# Revit family: Sanitary_Toilet-Cisterns_Sanindusa_Urby-60-Cistern-With-Dual-Flush-Mechanism
name_source: partatom
category: Plumbing Fixtures
revit_build: Autodesk Revit 2018 (Build: 20170223_1515(x64)
units: mm (PartAtom-declared; Revit-internal decimal feet)

## family parameters
Always vertical = Yes
Cut with Voids When Loaded = No
Host = Wall
OmniClass Number = 23.45.00.00
OmniClass Title = Sanitary, Laundry, and Cleaning Equipment
Part Type = Normal
Room Calculation Point = No
Round Connector Dimension = Use Diameter
Shared = No

## types (1)
- SANINDUSA_Bottominletconnectioncisternwithdualflushmechanismforclosecoupledtoilet_140171004LM_379x155x432_Urb.y
    AssetType = Fixed
    CisternCapacity = 6 Lts
    CisternColor = white
    CisternHeight = LowLevel
    CisternMaterial = Vitreous China
    Color = white
    Constituents = Ceramic cistern with bottom inlet connection and dual flush mechanism included.
    Cost = 0 $
    Description = Bottom inlet connection cistern with dual flush mechanism for close coupled toilet
    Edition number = 1
    Element Type = CISTERN: A water storage unit attached to a sanitary terminal that is fitted with a device, operated automatically or by the user, that discharges water to cleanse a water closet (toilet) pan, urinal or slop hopper. (BS6100 330 5008)
    Features = Cistern with flushing mechanism for close coupled toilet.Flushing cistern volume: 6 litres. Mounting for dual flush. Large flush: 6 L. Small flush: 3 L. Connection to the water supply: on the bottom.
    Finish = gloss
    FlushRate = Lowerbound:3 Lts
Upperbound:6 Lts
Upperbound:5/6/7Lts
    FlushType = push
    Installation Instructions = https://www.tec.sanindusa.pt
    InstallationDate = 1900-12-31T23:59:59
    IsAutomaticFlush = FALSE
    IsSingleFlush = FALSE
    Manufacturer = www.sanindusa.pt
    ManufacturerName = Sanindusa
    ManufacturerURL = www.tec.sanindusa.pt
    Material = cistern-vitreous china
    ModelNumber = 140171004LM
    ModelReference = Urb.y
    Name = Urb.y 60 cistern with dual flush mechanism
    NominalHeight = 432 mm  [stored 1.41732 ft]
    NominalLength = 379 mm  [stored 1.24344 ft]
    NominalWidth = 155 mm  [stored 0.50853 ft]
    Pre-defined type (IFC) = CISTERN
    Product Guid = fc3231de-15f3-4122-95d8-c4d4401d5d01
    Product data url = https://bimobject.com
    ProductInformation = https://www.tec.sanindusa.pt
    ProductionYear = 2018
    Size = 379x155x432
    Type (IFC) = IfcSanitaryTerminalType
    URL = www.tec.sanindusa.pt
    Uniclass2015Code = Pr_40_20_93_89
    Uniclass2015Title = WC cisterns
    Uniclass2015Version = Products v1.6
    Version = 1
    WarrantyDescription = https://www.tec.sanindusa.pt
    WarrantyDurationParts = 5
    WarrantyDurationUnit = year
    WarrantyStartDate = 1900-12-31T23:59:59
    Weight = 10.00 kg
    X = 355 mm

note: [stored X ft] marks values corroborated as IEEE doubles in the binary element streams (Revit-internal decimal feet)

## geometry (parser evidence)
native form markers: Sweep x7
no freeform markers — native parametric forms only
